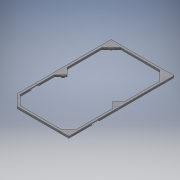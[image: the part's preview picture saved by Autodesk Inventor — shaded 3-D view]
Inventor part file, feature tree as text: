
AUTODESK INVENTOR PART (.ipt)
format: ipt  version: 2016 SP2 (Build 200236200, 236)  size: 166,400 bytes
history: native  units: mm
features: reference x15, extrude x3, sketch x3
ambient origin geometry x8: Origin, YZ Plane, XZ Plane, XY Plane, X Axis, Y Axis, Z Axis, Center Point
bodies: Volumenkörper1 (feature_tree)
feature tree (21):
  extrude  "Extrusion1"  Depth=3.0mm
  extrude  "Extrusion2"  Depth=3.0mm
  extrude  "Extrusion3"  TaperAngle=45.0deg  [1 undecoded]
  sketch  "Skizze1"  dims[d0=3.0mm d1=3.0mm]
  reference  "Referenz1"
  reference  "Referenz2"
  reference  "Referenz3"
  reference  "Referenz4"
  reference  "Referenz5"
  reference  "Referenz6"
  reference  "Referenz7"
  reference  "Referenz8"
  reference  "Referenz9"
  reference  "Referenz10"
  sketch  "Skizze2"  dims[d2=3.0mm d3=3.0mm]
  reference  "Referenz11"
  reference  "Referenz12"
  reference  "Referenz13"
  reference  "Referenz14"
  reference  "Referenz15"
  sketch  "Skizze3"  dims[d4=5.0mm d5=45.0deg d6=5.0mm d7=45.0deg d8=4.0mm d9=4.0mm d10=4.0mm d11=4.0mm d12=5.0mm d13=3.0mm d14=15.0mm d15=2.5mm d16=0.0mm d17=2.5mm d18=0.0mm d19=10.0mm d20=15.0mm d21=10.0mm d22=4.0mm d23=1.5mm d24=0.0mm]
note: 1 required parameter value undecoded (feature->parameter linkage not recoverable at this tier; creation-order binding heuristic only, values carry confidence <= 0.55)
